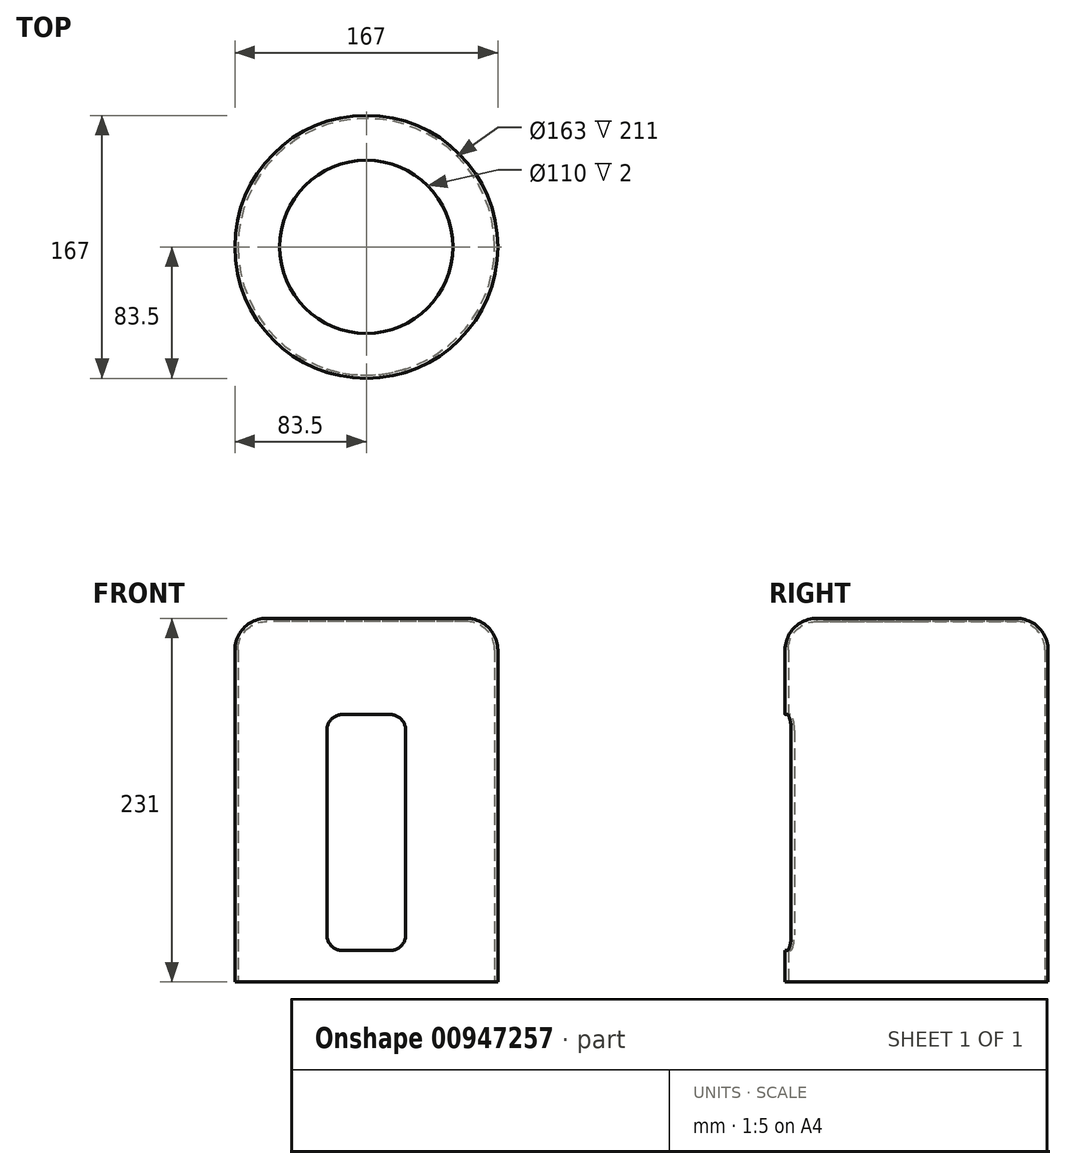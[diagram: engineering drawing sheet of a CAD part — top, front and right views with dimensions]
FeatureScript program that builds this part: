
annotation { "Feature Type Name" : "Feature", "Feature Type Description" : "" }
export const myFeature = defineFeature(function(context is Context, id is Id, definition is map)
    precondition{}
    {
        {
            var Q0;
            Q0=qCreatedBy(makeId("Top.planeOp"),FACE);
            var sketch = newSketch(context, id + "F0", { "sketchPlane" : qUnion([Q0])});
            skCircle(sketch, "E0", {"center": v(0, 0) * mm, "radius": 83.5 * mm});
            skSolve(sketch);
        }
        {
            var Q0;
            Q0=makeQuery(id+"F0.imprint","IMPRINT",FACE,{"disambiguationData":[TD([[makeQuery(id+"F0.imprint","IMPRINT",EDGE,{"derivedFrom":sQuery(id+"F0.wireOp",EDGE,"E0")}),1.0]])]});
            extrude(context, id + "F1", {"entities" : qUnion([Q0]), "depth" : 231 * mm, "offsetDistance" : 25 * mm});
        }
        {
            var Q0;
            Q0=makeQuery(id+"F1.opExtrude","CAP_EDGE",EDGE,{"disambiguationData":[OSD([sQuery(id+"F0.wireOp",EDGE,"E0")])],"isStart":false});
            fillet(context, id + "F2", {"entities" : qUnion([Q0]), "radius" : 20 * mm, "tangentPropagation" : true, "allowEdgeOverflow" : false});
        }
        {
            var Q0;
            Q0=makeQuery(id+"F1.opExtrude","CAP_FACE",FACE,{"disambiguationData":[OSD([sQuery(id+"F0.wireOp",EDGE,"E0")])],"isStart":true});
            shell(context, id + "F3", {"entities" : qUnion([Q0]), "thickness" : 2 * mm});
        }
        {
            var Q0;
            Q0=qCreatedBy(makeId("Front.planeOp"),FACE);
            var sketch = newSketch(context, id + "F4", { "sketchPlane" : qUnion([Q0])});
            skLineSegment(sketch, "E1.bottom", {"start": v(15, 20) * mm, "end": v(-15, 20) * mm});
            skLineSegment(sketch, "E1.top", {"start": v(15, 170) * mm, "end": v(-15, 170) * mm});
            skLineSegment(sketch, "E1.left", {"start": v(25, 30) * mm, "end": v(25, 160) * mm});
            skLineSegment(sketch, "E1.right", {"start": v(-25, 30) * mm, "end": v(-25, 160) * mm});
            skPoint(sketch, "E1.middle", {"position": v(0, 95) * mm});
            skPoint(sketch, "E2.visualSharp", {"position": v(-25, 170) * mm});
            skArc(sketch, "E2.filletArc", {"start": v(-15, 170) * mm, "mid": v(-22.07, 167.07) * mm, "end": v(-25, 160) * mm});
            skPoint(sketch, "E3.visualSharp", {"position": v(25, 170) * mm});
            skArc(sketch, "E3.filletArc", {"start": v(25, 160) * mm, "mid": v(22.07, 167.07) * mm, "end": v(15, 170) * mm});
            skPoint(sketch, "E4.visualSharp", {"position": v(-25, 20) * mm});
            skArc(sketch, "E4.filletArc", {"start": v(-25, 30) * mm, "mid": v(-22.07, 22.93) * mm, "end": v(-15, 20) * mm});
            skPoint(sketch, "E5.visualSharp", {"position": v(25, 20) * mm});
            skArc(sketch, "E5.filletArc", {"start": v(15, 20) * mm, "mid": v(22.07, 22.93) * mm, "end": v(25, 30) * mm});
            skSolve(sketch);
        }
        {
            var Q0;
            Q0 = qSketchRegion(id + "F4", true);
            var Q1;
            Q1=makeQuery(id+"F1.opExtrude","SWEPT_FACE",FACE,{"disambiguationData":[OSD([sQuery(id+"F0.wireOp",EDGE,"E0")])]});
            extrude(context, id + "F5", {"entities" : qUnion([Q0]), "operationType" : NewBodyOperationType.REMOVE, "endBound" : BoundingType.UP_TO_SURFACE, "depth" : 25 * mm, "endBoundEntityFace" : qUnion([Q1]), "offsetDistance" : 25 * mm});
        }
        {
            var Q0;
            Q0=makeQuery(id+"F1.opExtrude","CAP_FACE",FACE,{"disambiguationData":[OSD([sQuery(id+"F0.wireOp",EDGE,"E0")])],"isStart":false});
            var sketch = newSketch(context, id + "F6", { "sketchPlane" : qUnion([Q0])});
            skCircle(sketch, "E6", {"center": v(0, 0) * mm, "radius": 55 * mm});
            skSolve(sketch);
        }
        {
            var Q0;
            Q0=makeQuery(id+"F6.imprint","IMPRINT",FACE,{"disambiguationData":[TD([[makeQuery(id+"F6.imprint","IMPRINT",EDGE,{"derivedFrom":sQuery(id+"F6.wireOp",EDGE,"E6")}),1.0]])]});
            extrude(context, id + "F7", {"entities" : qUnion([Q0]), "operationType" : NewBodyOperationType.REMOVE, "oppositeDirection" : true, "depth" : 25 * mm, "offsetDistance" : 25 * mm});
        }
    });
